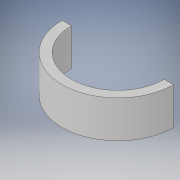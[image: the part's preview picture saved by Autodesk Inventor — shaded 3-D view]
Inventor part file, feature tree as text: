
AUTODESK INVENTOR PART (.ipt)
format: ipt  version: 2019 (Build 230136000, 136)  size: 96,256 bytes
history: native  units: in
note: dims shown in document units (in); Inventor stores cm internally (conversion verified against a paired STEP export)
features: extrude x1, sketch x1
ambient origin geometry x8: Origin, YZ Plane, XZ Plane, XY Plane, X Axis, Y Axis, Z Axis, Center Point
bodies: Solid1 (feature_tree)
feature tree (2):
  extrude  "Extrusion1"  Depth=1.5in
  sketch  "Sketch1"  dims[d0=1.25in d1=1.5in d2=1.0in d3=0.0in]
